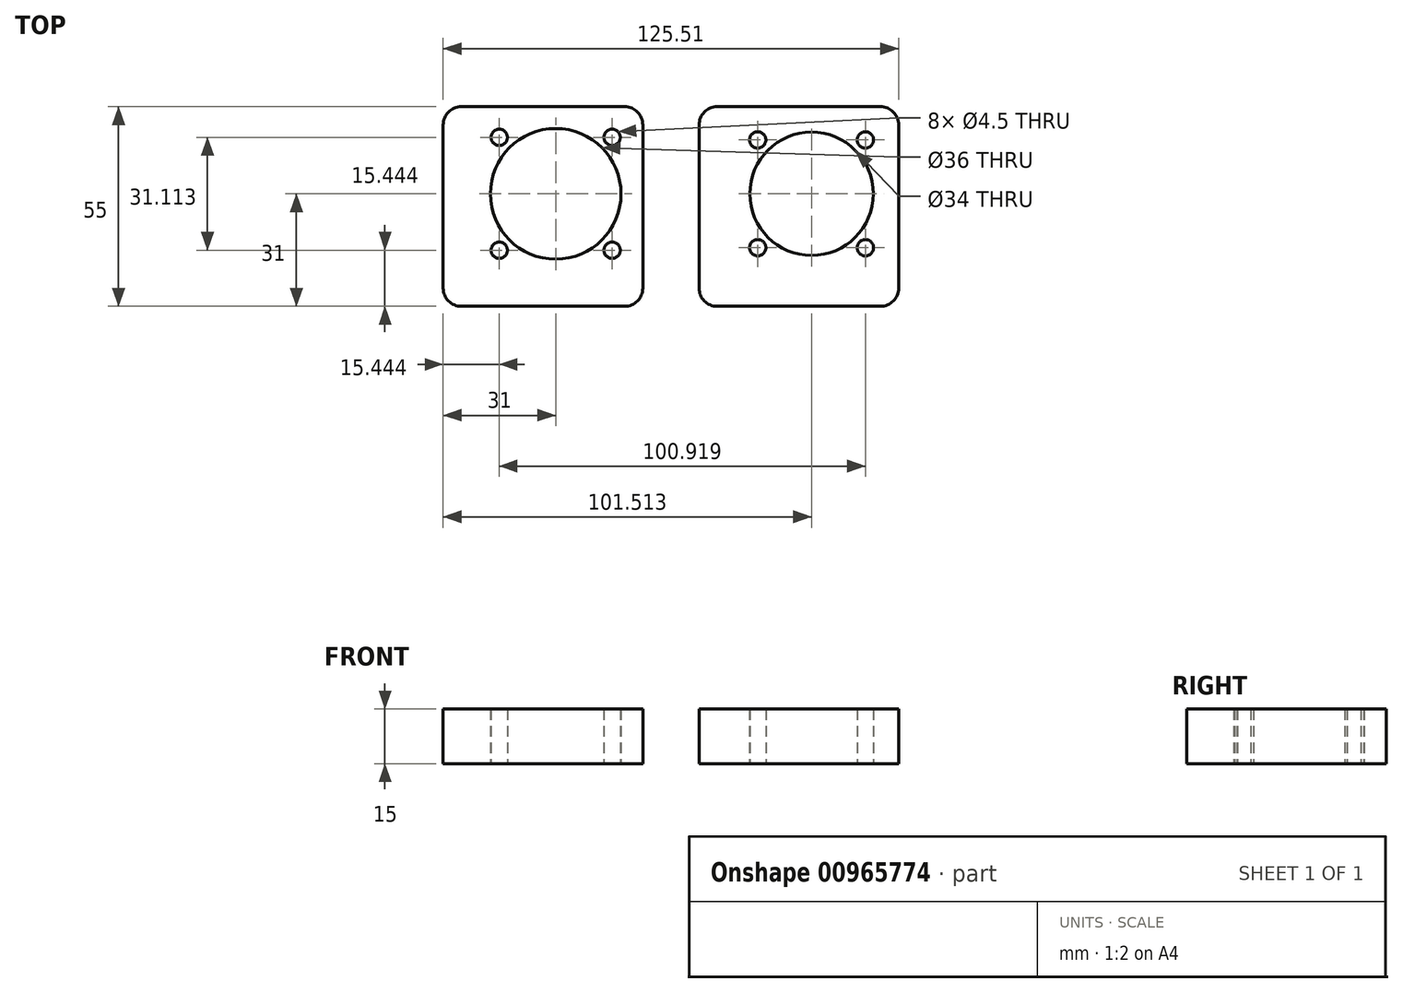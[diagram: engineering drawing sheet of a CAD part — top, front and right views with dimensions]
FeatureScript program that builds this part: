
annotation { "Feature Type Name" : "Feature", "Feature Type Description" : "" }
export const myFeature = defineFeature(function(context is Context, id is Id, definition is map)
    precondition{}
    {
        {
            var Q0;
            Q0=qCreatedBy(makeId("Top.planeOp"),FACE);
            var sketch = newSketch(context, id + "F0", { "sketchPlane" : qUnion([Q0])});
            skLineSegment(sketch, "E0.bottom", {"start": v(27.5, -27.5) * mm, "end": v(-27.5, -27.5) * mm});
            skLineSegment(sketch, "E0.top", {"start": v(27.5, 27.5) * mm, "end": v(-27.5, 27.5) * mm});
            skLineSegment(sketch, "E0.left", {"start": v(27.5, -27.5) * mm, "end": v(27.5, 27.5) * mm});
            skLineSegment(sketch, "E0.right", {"start": v(-27.5, -27.5) * mm, "end": v(-27.5, 27.5) * mm});
            skPoint(sketch, "E0.middle", {"position": v(0, 0) * mm});
            skLineSegment(sketch, "E1.bottom", {"start": v(25.5, -18.5) * mm, "end": v(-18.5, -18.5) * mm, "construction": true});
            skLineSegment(sketch, "E1.top", {"start": v(25.5, 25.5) * mm, "end": v(-18.5, 25.5) * mm, "construction": true});
            skLineSegment(sketch, "E1.left", {"start": v(25.5, -18.5) * mm, "end": v(25.5, 25.5) * mm, "construction": true});
            skLineSegment(sketch, "E1.right", {"start": v(-18.5, -18.5) * mm, "end": v(-18.5, 25.5) * mm, "construction": true});
            skPoint(sketch, "E1.middle", {"position": v(3.5, 3.5) * mm});
            skCircle(sketch, "E2", {"center": v(3.5, 3.5) * mm, "radius": 22 * mm, "construction": true});
            skCircle(sketch, "E3", {"center": v(-12.06, -12.06) * mm, "radius": 2.25 * mm});
            skLineSegment(sketch, "E4", {"start": v(-18.5, -18.5) * mm, "end": v(25.5, 25.5) * mm, "construction": true});
            skLineSegment(sketch, "E5", {"start": v(25.5, -18.5) * mm, "end": v(-18.5, 25.5) * mm, "construction": true});
            skCircle(sketch, "E6", {"center": v(-12.06, 19.06) * mm, "radius": 2.25 * mm});
            skCircle(sketch, "E7", {"center": v(19.06, 19.06) * mm, "radius": 2.25 * mm});
            skCircle(sketch, "E8", {"center": v(19.06, -12.06) * mm, "radius": 2.25 * mm});
            skCircle(sketch, "E9", {"center": v(3.5, 3.5) * mm, "radius": 18 * mm});
            skSolve(sketch);
        }
        {
            var Q0;
            Q0=qCreatedBy(makeId("Top.planeOp"),FACE);
            var sketch = newSketch(context, id + "F1", { "sketchPlane" : qUnion([Q0])});
            skLineSegment(sketch, "E10.bottom", {"start": v(98.01, -27.5) * mm, "end": v(43.01, -27.5) * mm});
            skLineSegment(sketch, "E10.top", {"start": v(98.01, 27.5) * mm, "end": v(43.01, 27.5) * mm});
            skLineSegment(sketch, "E10.left", {"start": v(98.01, -27.5) * mm, "end": v(98.01, 27.5) * mm});
            skLineSegment(sketch, "E10.right", {"start": v(43.01, -27.5) * mm, "end": v(43.01, 27.5) * mm});
            skPoint(sketch, "E10.middle", {"position": v(70.51, 0) * mm});
            skPoint(sketch, "E11.0", {"position": v(74.01, 3.5) * mm});
            skCircle(sketch, "E12", {"center": v(74.01, 3.5) * mm, "radius": 17 * mm});
            skCircle(sketch, "E13", {"center": v(74.01, 3.5) * mm, "radius": 21 * mm, "construction": true});
            skLineSegment(sketch, "E14.bottom", {"start": v(95.01, -17.5) * mm, "end": v(53.01, -17.5) * mm, "construction": true});
            skLineSegment(sketch, "E14.top", {"start": v(95.01, 24.5) * mm, "end": v(53.01, 24.5) * mm, "construction": true});
            skLineSegment(sketch, "E14.left", {"start": v(95.01, -17.5) * mm, "end": v(95.01, 24.5) * mm, "construction": true});
            skLineSegment(sketch, "E14.right", {"start": v(53.01, -17.5) * mm, "end": v(53.01, 24.5) * mm, "construction": true});
            skLineSegment(sketch, "E15", {"start": v(53.01, 24.5) * mm, "end": v(95.01, -17.5) * mm, "construction": true});
            skLineSegment(sketch, "E16", {"start": v(95.01, 24.5) * mm, "end": v(53.01, -17.5) * mm, "construction": true});
            skCircle(sketch, "E17", {"center": v(59.16, 18.35) * mm, "radius": 2.25 * mm});
            skCircle(sketch, "E18", {"center": v(88.86, 18.35) * mm, "radius": 2.25 * mm});
            skCircle(sketch, "E19", {"center": v(59.16, -11.35) * mm, "radius": 2.25 * mm});
            skCircle(sketch, "E20", {"center": v(88.86, -11.35) * mm, "radius": 2.25 * mm});
            skPoint(sketch, "E21.0", {"position": v(121.33, 10.53) * mm});
            skSolve(sketch);
        }
        {
            var Q0;
            Q0 = qSketchRegion(id + "F0", true);
            var Q1;
            Q1 = qSketchRegion(id + "F1", true);
            extrude(context, id + "F2", {"entities" : qUnion([Q0, Q1]), "depth" : 15 * mm, "offsetDistance" : 25 * mm});
        }
        {
            var Q0;
            Q0=makeQuery(id+"F2.opExtrude","SWEPT_EDGE",EDGE,{"disambiguationData":[OSD([sQuery(id+"F0.wireOp",EDGE,"E0.bottom"),sQuery(id+"F0.wireOp",EDGE,"E0.right")])]});
            var Q1;
            Q1=makeQuery(id+"F2.opExtrude","SWEPT_EDGE",EDGE,{"disambiguationData":[OSD([sQuery(id+"F0.wireOp",EDGE,"E0.bottom"),sQuery(id+"F0.wireOp",EDGE,"E0.left")])]});
            var Q2;
            Q2=makeQuery(id+"F2.opExtrude","SWEPT_EDGE",EDGE,{"disambiguationData":[OSD([sQuery(id+"F0.wireOp",EDGE,"E0.top"),sQuery(id+"F0.wireOp",EDGE,"E0.left")])]});
            var Q3;
            Q3=makeQuery(id+"F2.opExtrude","SWEPT_EDGE",EDGE,{"disambiguationData":[OSD([sQuery(id+"F0.wireOp",EDGE,"E0.top"),sQuery(id+"F0.wireOp",EDGE,"E0.right")])]});
            var Q4;
            Q4=makeQuery(id+"F2.opExtrude","SWEPT_EDGE",EDGE,{"disambiguationData":[OSD([sQuery(id+"F1.wireOp",EDGE,"E10.top"),sQuery(id+"F1.wireOp",EDGE,"E10.right")])]});
            var Q5;
            Q5=makeQuery(id+"F2.opExtrude","SWEPT_EDGE",EDGE,{"disambiguationData":[OSD([sQuery(id+"F1.wireOp",EDGE,"E10.top"),sQuery(id+"F1.wireOp",EDGE,"E10.left")])]});
            var Q6;
            Q6=makeQuery(id+"F2.opExtrude","SWEPT_EDGE",EDGE,{"disambiguationData":[OSD([sQuery(id+"F1.wireOp",EDGE,"E10.bottom"),sQuery(id+"F1.wireOp",EDGE,"E10.right")])]});
            var Q7;
            Q7=makeQuery(id+"F2.opExtrude","SWEPT_EDGE",EDGE,{"disambiguationData":[OSD([sQuery(id+"F1.wireOp",EDGE,"E10.bottom"),sQuery(id+"F1.wireOp",EDGE,"E10.left")])]});
            fillet(context, id + "F3", {"entities" : qUnion([Q0, Q1, Q2, Q3, Q4, Q5, Q6, Q7]), "radius" : 5 * mm, "tangentPropagation" : true, "allowEdgeOverflow" : false});
        }
    });
